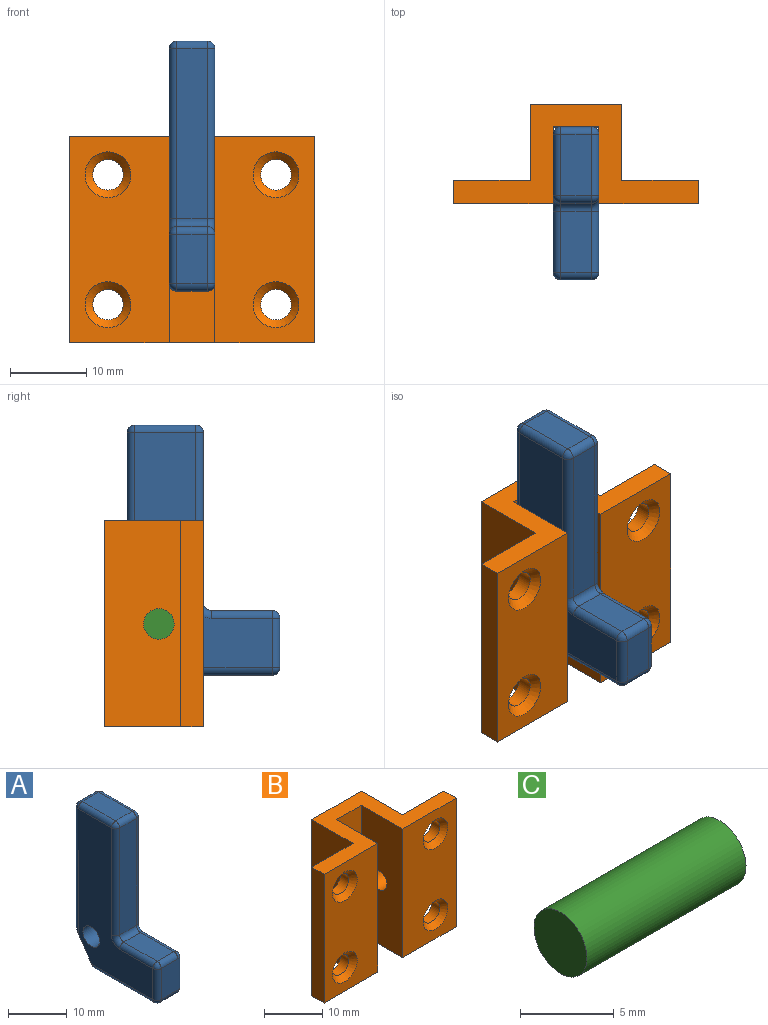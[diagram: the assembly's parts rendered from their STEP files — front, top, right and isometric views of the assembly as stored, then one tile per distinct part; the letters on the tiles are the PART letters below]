
ASSEMBLY  parts=3 mates=2
PART A: 38 faces, bbox 6x20x32.7 mm
  f0: plane 30.73x18mm, normal (1,0,0), area 290.9mm2, adj f4,f6,f10,f13,f16,f20,f25,f26
  f1: plane 30.73x18mm, normal (-1,0,0), area 290.9mm2, adj f4,f6,f15,f22,f23,f32,f33,f35
  f2: plane 6.46x4mm, normal (0,-1,0), area 25.9mm2, adj f13,f14,f21,f22
  f3: plane 8x4mm, normal (0,0,1), area 32mm2, adj f24,f25,f33,f34
  f4: plane 6.85x6.02mm, normal (0,0.83,-0.56), area 48.8mm2, adj f0,f1,f5,f10,f12,f15,f16,f23
  f5: plane 24.45x4mm, normal (0,1,0), area 97.8mm2, adj f4,f16,f23,f24
  f6: cylinder r=2mm len=6mm, axis (1,0,0), area 75.4mm2, adj f0,f1
  f7: plane 13.52x4mm, normal (0,0,-1), area 54.1mm2, adj f10,f12,f14,f15
  f8: plane 22.26x4mm, normal (0,-1,0), area 89.1mm2, adj f26,f31,f34,f37
  f9: plane 8x4mm, normal (0,0,1), area 32mm2, adj f20,f21,f31,f32
  f10: cylinder r=1mm len=14.73mm, axis (0,1,0), area 22.3mm2, adj f0,f4,f7,f11,f12
  f11: sphere r=1mm, area 1.6mm2, adj f10,f13,f14
  f12: cylinder r=1mm len=5.65mm, axis (1,0,0), area 4.8mm2, adj f4,f7,f10,f15
  f13: cylinder r=1mm len=6.46mm, axis (0,0,1), area 10.2mm2, adj f0,f2,f11,f17
  f14: cylinder r=1mm len=4mm, axis (1,0,0), area 6.3mm2, adj f2,f7,f11,f18
  f15: cylinder r=1mm len=14.73mm, axis (0,1,0), area 22.3mm2, adj f1,f4,f7,f12,f18
  f16: cylinder r=1mm len=25.92mm, axis (0,0,-1), area 39.3mm2, adj f0,f4,f5,f19
  f17: sphere r=1mm, area 1.6mm2, adj f13,f20,f21
  f18: sphere r=1mm, area 1.6mm2, adj f14,f15,f22
  f19: sphere r=1mm, area 1.6mm2, adj f16,f24,f25
  f20: cylinder r=1mm len=8mm, axis (0,-1,0), area 12.6mm2, adj f0,f9,f17,f27
  f21: cylinder r=1mm len=4mm, axis (-1,0,0), area 6.3mm2, adj f2,f9,f17,f28
  f22: cylinder r=1mm len=6.46mm, axis (0,0,-1), area 10.2mm2, adj f1,f2,f18,f28
  f23: cylinder r=1mm len=25.92mm, axis (0,0,1), area 39.3mm2, adj f1,f4,f5,f29
  f24: cylinder r=1mm len=4mm, axis (1,0,0), area 6.3mm2, adj f3,f5,f19,f29
  f25: cylinder r=1mm len=8mm, axis (0,-1,0), area 12.6mm2, adj f0,f3,f19,f30
  f26: cylinder r=1mm len=22.26mm, axis (0,0,-1), area 35mm2, adj f0,f8,f27,f30
  f27: torus R=2mm, axis (1,0,0), area 3.4mm2, adj f0,f20,f26,f31
  f28: sphere r=1mm, area 1.6mm2, adj f21,f22,f32
  f29: sphere r=1mm, area 1.6mm2, adj f23,f24,f33
  f30: sphere r=1mm, area 1.6mm2, adj f25,f26,f34
  f31: cylinder r=1mm len=4mm, axis (-1,0,0), area 6.3mm2, adj f8,f9,f27,f35
  f32: cylinder r=1mm len=8mm, axis (0,-1,0), area 12.6mm2, adj f1,f9,f28,f35
  f33: cylinder r=1mm len=8mm, axis (0,1,0), area 12.6mm2, adj f1,f3,f29,f36
  f34: cylinder r=1mm len=4mm, axis (1,0,0), area 6.3mm2, adj f3,f8,f30,f36
  f35: torus R=2mm, axis (1,0,0), area 3.4mm2, adj f1,f31,f32,f37
  f36: sphere r=1mm, area 1.6mm2, adj f33,f34,f37
  f37: cylinder r=1mm len=22.26mm, axis (0,0,-1), area 35mm2, adj f1,f8,f35,f36
PART B: 24 faces, bbox 32x13x27 mm
  f0: plane 27x3mm, normal (-1,0,0), area 81mm2, adj f1,f11,f12,f15
  f1: plane 27x13mm, normal (0,-1,0), area 294.5mm2, adj f0,f2,f12,f15,f22,f23
  f2: plane 27x10mm, normal (1,0,0), area 257.4mm2, adj f1,f3,f12,f13,f15
  f3: plane 27x6mm, normal (0,-1,0), area 162mm2, adj f2,f4,f12,f15
  f4: plane 27x10mm, normal (-1,0,0), area 257.4mm2, adj f3,f5,f12,f14,f15
  f5: plane 27x13mm, normal (0,-1,0), area 294.5mm2, adj f4,f6,f12,f15,f20,f21
  f6: plane 27x3mm, normal (1,0,0), area 81mm2, adj f5,f7,f12,f15
  f7: plane 27x10mm, normal (0,1,0), area 244.9mm2, adj f6,f8,f12,f15,f18,f19
  f8: plane 27x10mm, normal (1,0,0), area 257.4mm2, adj f7,f9,f12,f14,f15
  f9: plane 27x12mm, normal (0,1,0), area 324mm2, adj f8,f10,f12,f15
  f10: plane 27x10mm, normal (-1,0,0), area 257.4mm2, adj f9,f11,f12,f13,f15
  f11: plane 27x10mm, normal (0,1,0), area 244.9mm2, adj f0,f10,f12,f15,f16,f17
  f12: plane 32x13mm, normal (0,0,1), area 156mm2, adj f0,f1,f2,f3,f4,f5,f6,f7
  f13: cylinder r=2mm len=4mm, axis (1,0,0), area 37.7mm2, adj f2,f10
  f14: cylinder r=2mm len=4mm, axis (1,0,0), area 37.7mm2, adj f4,f8
  f15: plane 32x13mm, normal (0,0,-1), area 156mm2, adj f0,f1,f2,f3,f4,f5,f6,f7
  f16: cylinder r=2mm len=4mm, axis (0,-1,0), area 25.1mm2, adj f11,f23
  f17: cylinder r=2mm len=4mm, axis (0,-1,0), area 25.1mm2, adj f11,f22
  f18: cylinder r=2mm len=4mm, axis (0,-1,0), area 25.1mm2, adj f7,f21
  f19: cylinder r=2mm len=4mm, axis (0,-1,0), area 25.1mm2, adj f7,f20
  f20: cone r=2mm half-angle=45deg, axis (0,-1,0), area 22.2mm2, adj f5,f19
  f21: cone r=2mm half-angle=45deg, axis (0,-1,0), area 22.2mm2, adj f5,f18
  f22: cone r=2mm half-angle=45deg, axis (0,-1,0), area 22.2mm2, adj f1,f17
  f23: cone r=2mm half-angle=45deg, axis (0,-1,0), area 22.2mm2, adj f1,f16
PART C: 3 faces, bbox 12x4x4 mm
  f0: cylinder r=2mm len=12mm, axis (-1,0,0), area 150.8mm2, adj f1,f2
  f1: plane 4x4mm, normal (1,0,0), area 12.6mm2, adj f0
  f2: plane 4x4mm, normal (-1,0,0), area 12.6mm2, adj f0
PLACE A rot(axis=(-1,0,0),0deg) t=(0,-3.49,1.07)mm
PLACE B t=(0,-3.49,1.07)mm fixed
PLACE C rot(axis=(1,0,0),0deg) t=(0,-3.49,1.07)mm
MATE revolute A.f6 <-> C.f0  axis (1,0,0) through (0,-10.66,-4.96)mm
MATE revolute C.f0 <-> B.f13  axis (1,0,0) through (6,-10.66,-4.96)mm
